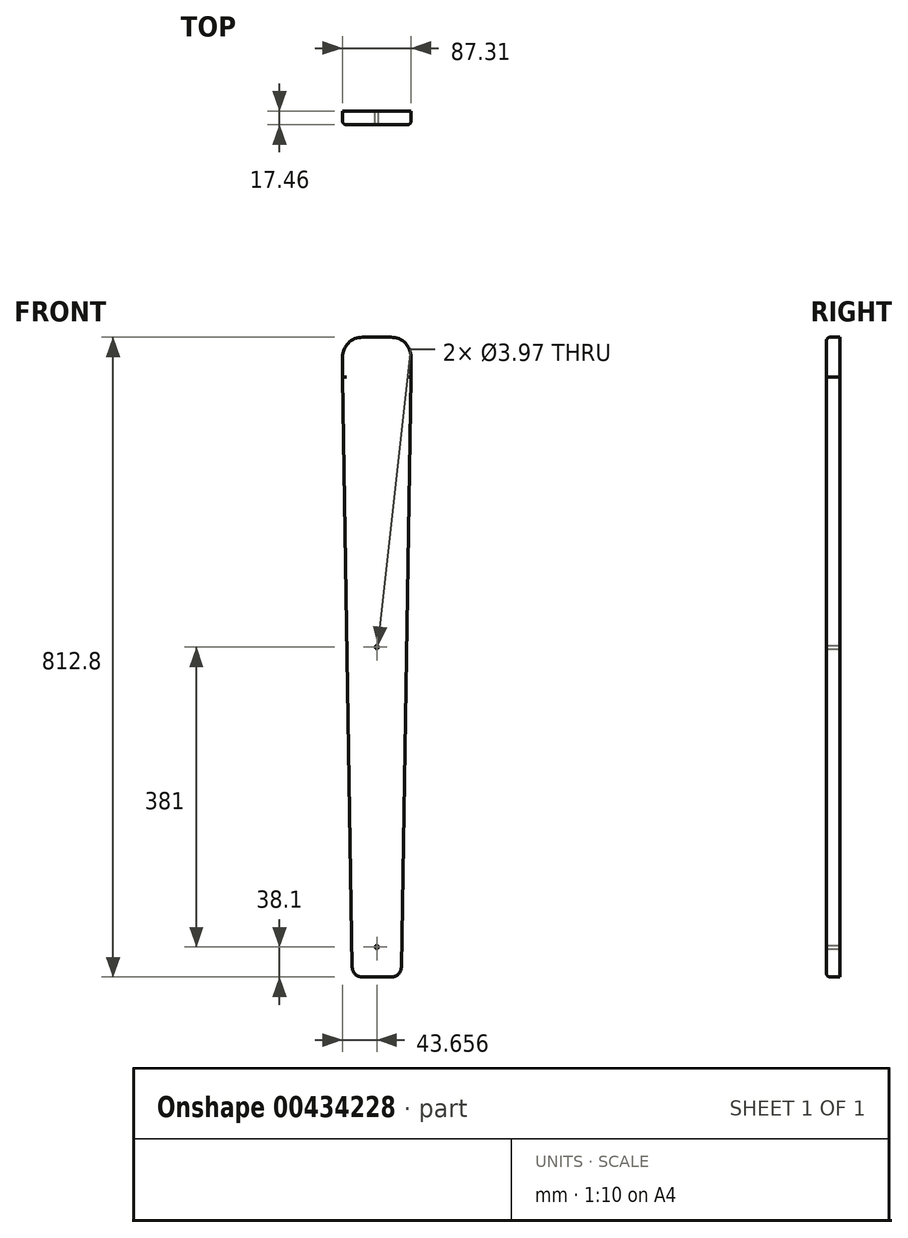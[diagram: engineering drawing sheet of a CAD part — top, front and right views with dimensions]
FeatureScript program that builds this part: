
annotation { "Feature Type Name" : "Feature", "Feature Type Description" : "" }
export const myFeature = defineFeature(function(context is Context, id is Id, definition is map)
    precondition{}
    {
        {
            var Q0;
            Q0=qCreatedBy(makeId("Front.planeOp"),FACE);
            var sketch = newSketch(context, id + "F0", { "sketchPlane" : qUnion([Q0])});
            skLineSegment(sketch, "E0.top", {"start": v(25.4, 812.8) * mm, "end": v(61.91, 812.8) * mm});
            skPoint(sketch, "E1.visualSharp", {"position": v(0, 812.8) * mm});
            skArc(sketch, "E1.filletArc", {"start": v(25.4, 812.8) * mm, "mid": v(7.44, 805.36) * mm, "end": v(0, 787.4) * mm});
            skPoint(sketch, "E2.visualSharp", {"position": v(87.31, 812.8) * mm});
            skArc(sketch, "E2.filletArc", {"start": v(87.31, 787.4) * mm, "mid": v(79.87, 805.36) * mm, "end": v(61.91, 812.8) * mm});
            skLineSegment(sketch, "E3", {"start": v(0, 787.4) * mm, "end": v(0, 762) * mm});
            skLineSegment(sketch, "E4", {"start": v(87.31, 787.4) * mm, "end": v(87.31, 762) * mm});
            skLineSegment(sketch, "E5", {"start": v(0, 762) * mm, "end": v(12.5, 12.49) * mm});
            skLineSegment(sketch, "E6", {"start": v(25.2, 0) * mm, "end": v(62.12, 0) * mm});
            skLineSegment(sketch, "E7", {"start": v(74.82, 12.49) * mm, "end": v(87.31, 762) * mm});
            skLineSegment(sketch, "E8", {"start": v(87.31, 812.8) * mm, "end": v(61.91, 812.8) * mm, "construction": true});
            skLineSegment(sketch, "E9", {"start": v(25.4, 812.8) * mm, "end": v(0, 812.8) * mm, "construction": true});
            skLineSegment(sketch, "E10", {"start": v(0, 812.8) * mm, "end": v(0, 787.4) * mm, "construction": true});
            skLineSegment(sketch, "E11", {"start": v(87.31, 812.8) * mm, "end": v(87.31, 787.4) * mm, "construction": true});
            skLineSegment(sketch, "E12", {"start": v(0, 762) * mm, "end": v(0, 0) * mm, "construction": true});
            skLineSegment(sketch, "E13", {"start": v(87.31, 762) * mm, "end": v(87.31, 0) * mm, "construction": true});
            skPoint(sketch, "E14.visualSharp", {"position": v(12.7, 0) * mm});
            skArc(sketch, "E14.filletArc", {"start": v(12.5, 12.49) * mm, "mid": v(16.28, 3.65) * mm, "end": v(25.2, 0) * mm});
            skPoint(sketch, "E15.visualSharp", {"position": v(74.61, 0) * mm});
            skArc(sketch, "E15.filletArc", {"start": v(62.12, 0) * mm, "mid": v(71.03, 3.65) * mm, "end": v(74.82, 12.49) * mm});
            skLineSegment(sketch, "E16", {"start": v(0, 0) * mm, "end": v(25.2, 0) * mm, "construction": true});
            skLineSegment(sketch, "E17", {"start": v(62.12, 0) * mm, "end": v(87.31, 0) * mm, "construction": true});
            skCircle(sketch, "E18", {"center": v(43.66, 38.1) * mm, "radius": 1.98 * mm});
            skPoint(sketch, "E18.centerSnap0", {"position": v(43.66, 0) * mm});
            skCircle(sketch, "E19", {"center": v(43.66, 419.1) * mm, "radius": 1.98 * mm});
            skSolve(sketch);
        }
        {
            var Q0;
            Q0 = qSketchRegion(id + "F0", true);
            extrude(context, id + "F1", {"entities" : qUnion([Q0]), "depth" : 17.46 * mm});
        }
        {
            var Q0;
            Q0=makeQuery(id+"F1.opExtrude","CAP_EDGE",EDGE,{"disambiguationData":[OSD([sQuery(id+"F0.wireOp",EDGE,"E5")])],"isStart":false});
            var Q1;
            Q1=makeQuery(id+"F1.opExtrude","CAP_EDGE",EDGE,{"disambiguationData":[OSD([sQuery(id+"F0.wireOp",EDGE,"E1.filletArc")])],"isStart":false});
            fillet(context, id + "F2", {"entities" : qUnion([Q0, Q1]), "radius" : 5.08 * mm, "tangentPropagation" : true, "allowEdgeOverflow" : false});
        }
    });
